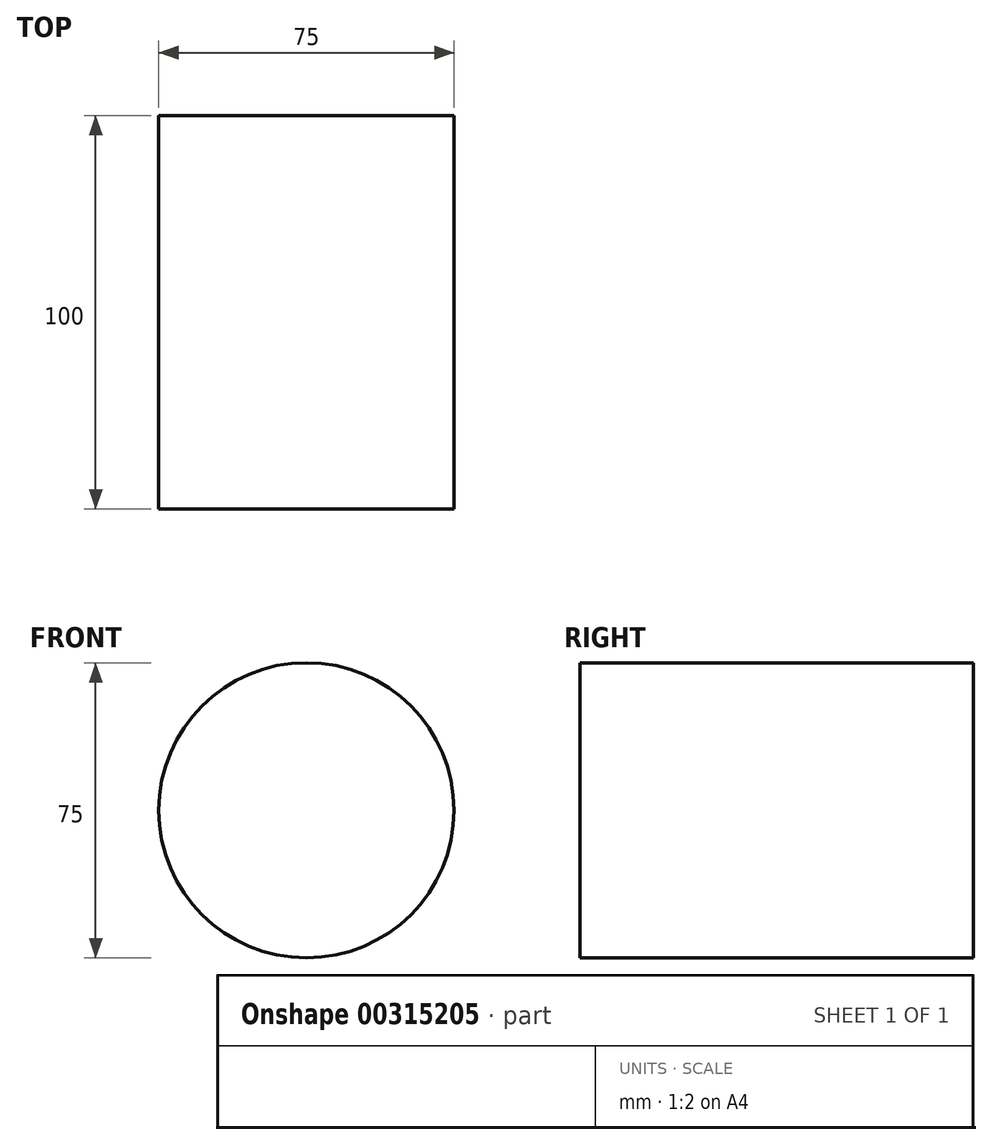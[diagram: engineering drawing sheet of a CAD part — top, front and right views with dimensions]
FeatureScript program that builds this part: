
annotation { "Feature Type Name" : "Feature", "Feature Type Description" : "" }
export const myFeature = defineFeature(function(context is Context, id is Id, definition is map)
    precondition{}
    {
        {
            var Q0;
            Q0=qCreatedBy(makeId("Front.planeOp"),FACE);
            var sketch = newSketch(context, id + "F0", { "sketchPlane" : qUnion([Q0])});
            skCircle(sketch, "E0", {"center": v(0, 0) * mm, "radius": 37.5 * mm});
            skSolve(sketch);
        }
        {
            var Q0;
            Q0 = qSketchRegion(id + "F0", true);
            extrude(context, id + "F1", {"entities" : qUnion([Q0]), "endBound" : BoundingType.SYMMETRIC, "depth" : 100 * mm});
        }
    });
